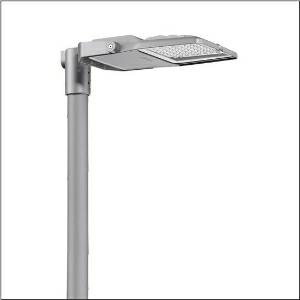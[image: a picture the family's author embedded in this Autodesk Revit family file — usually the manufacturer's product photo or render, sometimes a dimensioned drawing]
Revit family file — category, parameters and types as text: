
# Revit family: floodlight_fl_21_mini___pl61_5xa7775d2c3a_f3a4
name_source: partatom
category: Lighting Fixtures
units: mm (PartAtom-declared; Revit-internal decimal feet)

## family parameters
Cut with Voids When Loaded = No
Host = Face
Light Source = No
Part Type = Normal
Room Calculation Point = No
Round Connector Dimension = Use Diameter
Shared = No

## types (1)
- --- (1 x LED, 17510 lm, 142.9 W, 3000K)
    Apparent Load = 143 VA
    CIE Flux Codes = 33 65 98 100 100
    Color Rendering = 70
    Color Temperature = 3000K
    Default Elevation = 1800 mm
    Description = Floodlight FL 21 mini, floodlight, primary light control with lens, of PMMA, primary optical cover: protective disc, of toughened safety glass, transparent, light distribution: PL61, light emission: direct distribution, installation type: surface-mounted, LED, High Power LED, rated luminous flux: 17.510lm, luminous efficacy: 123lm/W, light colour: 730, colour temperature: 3000K, control gear: Smart Interface (Zhaga), control: flexible luminous flux parameterisation, time-dependent luminous flux control, constant luminous flux control, overheat protection, pre-setting: logarithmic dimming characteristic, with terminal, 6-pole, mains connection: 220..240V, AC, 50/60Hz, start of lifetime: 143W, end of service life: 151W, reduction: 63W, luminaire housing, of diecast aluminium, powder-coated, SITECO metallic grey (DB 702S), corrosivity category C5 mid according to DIN EN ISO 12944, suitable for swimming pools, chlorine-resistant, sealing non-destructively replaceable, please order mast flange separately, mast bracket, of steel, galvanised, powder-coated, SITECO metallic grey (DB 702S), Smart Interface above, protection rating (complete): IP66, insulation class (complete): insulation class II (safety insulation), certification: CE, ENEC, VDE, protection symbol: D, impact resistance: IK08, permissible operating ambient temperature: -40..+40°C, permissible operating ambient temperature for outdoor applications: -40..+50°C, standard: DIN EN 12944, LABS conformity tested according to VDMA 24364:2018-05, packaging unit: 1 piece

Light Distribution: PL61
    Height = 70 mm
    Lamp = 1 x LED
    Lamp Light Flux = 17510 lm
    Lamp Power = 142.9 W
    Lamp count = 1
    Length = 485 mm
    Luminous efficacy = 123 lm/W
    Manufacturer = Siteco
    ModVariant = No
    Model = 5XA7775D2C3A
    Number of Poles = 1
    OnlyDefault = Yes
    Power Factor = 1
    Product Name = Floodlight FL 21 mini | PL61
    Product group = floodlight | pylon annexe
    ProductGroupID = 6201
    Protection Class = Protection class II
    Protection Degree = IP 66
    RLX_Detail_Level = 1
    RLX_Emergency_Light_Flux = 0 lm
    RLX_Emergency_Type = 0
    RLX_Emergency_Type_DB = No
    RlxData = <blob elided: 101361 chars, md5=7af9860f>
    Socket = socket
    Standby Power = 0 W
    System Light Flux = 17510 lm
    System Power = 143 W
    Type Comments = factory setting: luminous flux: 100 % | dim-lin: 254 | 730 mA
    Type Image = l_1007125.jpg
    URL = http://relux.com
    VarID = @adj_171403
    Voltage = 0 V
    Weight = 0.00 kg
    Width = 337 mm

## geometry (parser evidence)
native form markers: Blend x4, Sweep x11
no freeform markers — native parametric forms only
